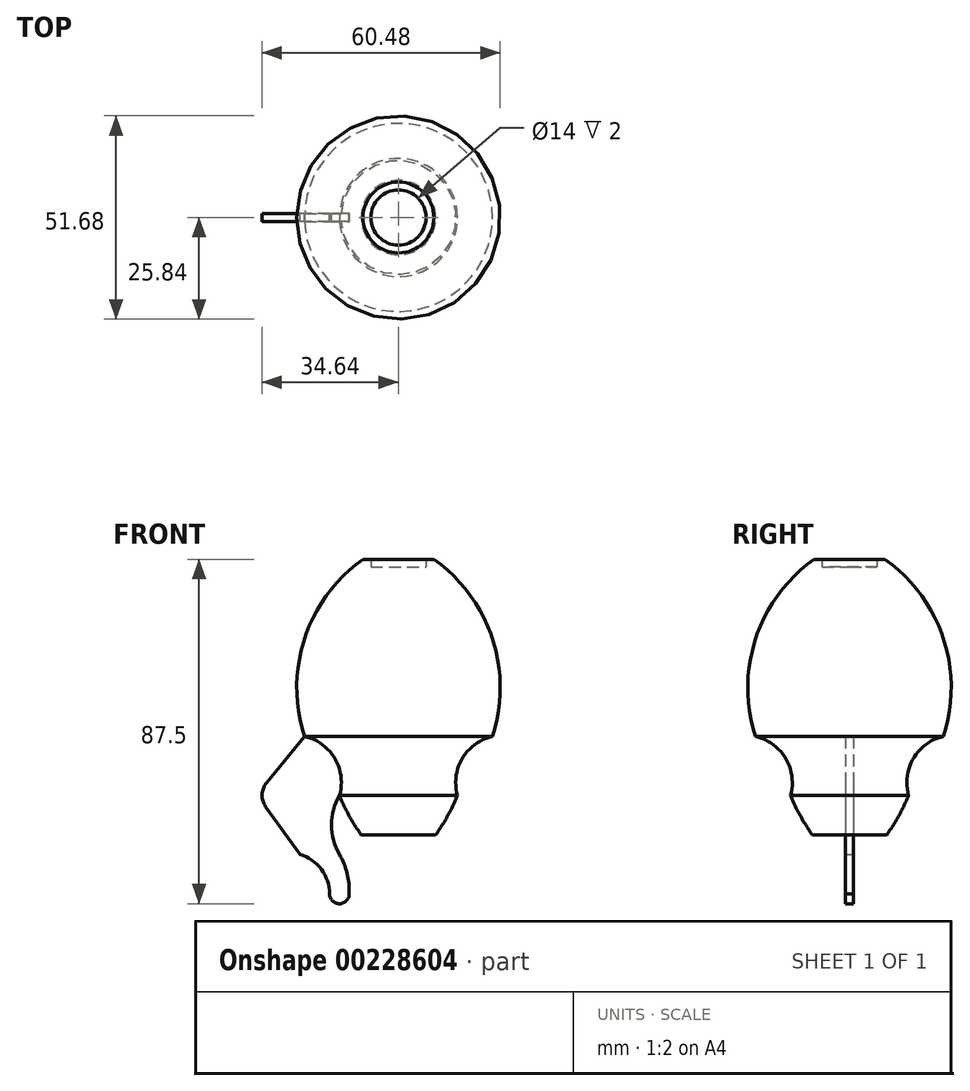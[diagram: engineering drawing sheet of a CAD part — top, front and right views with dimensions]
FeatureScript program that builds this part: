
annotation { "Feature Type Name" : "Feature", "Feature Type Description" : "" }
export const myFeature = defineFeature(function(context is Context, id is Id, definition is map)
    precondition{}
    {
        {
            var Q0;
            Q0=qCreatedBy(makeId("Front.planeOp"),FACE);
            var sketch = newSketch(context, id + "F0", { "sketchPlane" : qUnion([Q0])});
            skLineSegment(sketch, "E0", {"start": v(0, 0) * mm, "end": v(0, 78) * mm});
            skLineSegment(sketch, "E1", {"start": v(7, 80) * mm, "end": v(9, 80) * mm});
            skLineSegment(sketch, "E2", {"start": v(0, 20) * mm, "end": v(15, 20) * mm});
            skLineSegment(sketch, "E3", {"start": v(0, 35) * mm, "end": v(23.88, 35) * mm});
            skArc(sketch, "E4", {"start": v(23.88, 35) * mm, "mid": v(23.82, 59.94) * mm, "end": v(9, 80) * mm});
            skArc(sketch, "E5", {"start": v(23.88, 35) * mm, "mid": v(16.21, 29.41) * mm, "end": v(15, 20) * mm});
            skArc(sketch, "E6", {"start": v(0, 0) * mm, "mid": v(8.77, 9.05) * mm, "end": v(15, 20) * mm});
            skLineSegment(sketch, "E7", {"start": v(7, 80) * mm, "end": v(7, 78) * mm});
            skLineSegment(sketch, "E8", {"start": v(7, 78) * mm, "end": v(0, 78) * mm});
            skSolve(sketch);
        }
        {
            var Q0;
            Q0=makeQuery(id+"F0.imprint","IMPRINT",FACE,{"disambiguationData":[TD([[makeQuery(id+"F0.imprint","IMPRINT",EDGE,{"derivedFrom":sQuery(id+"F0.wireOp",EDGE,"E1")}),-1.0]])]});
            var Q1;
            {var subQ0=sQuery(id+"F0.wireOp",EDGE,"E2");Q1=makeQuery(id+"F0.imprint","IMPRINT",FACE,{"disambiguationData":[TD([[makeQuery(id+"F0.imprint","IMPRINT",EDGE,{"derivedFrom":subQ0}),1.0]])]});}
            var Q2;
            {var subQ2=sQuery(id+"F0.wireOp",EDGE,"E2");Q2=makeQuery(id+"F0.imprint","IMPRINT",FACE,{"disambiguationData":[TD([[makeQuery(id+"F0.imprint","IMPRINT",EDGE,{"derivedFrom":subQ2}),-1.0]])]});}
            var Q3;
            Q3=sQuery(id+"F0.wireOp",EDGE,"E0");
            revolve(context, id + "F1", {"entities" : qUnion([Q0, Q1, Q2]), "axis" : qUnion([Q3]), "revolveType" : RevolveType.FULL});
        }
        {
            var Q0;
            Q0=qCreatedBy(makeId("Front.planeOp"),FACE);
            var sketch = newSketch(context, id + "F2", { "sketchPlane" : qUnion([Q0])});
            skLineSegment(sketch, "E9.0", {"start": v(15, 20) * mm, "end": v(-15, 20) * mm});
            skLineSegment(sketch, "E10.0", {"start": v(23.88, 35) * mm, "end": v(-23.88, 35) * mm});
            skLineSegment(sketch, "E11", {"start": v(-23.88, 35) * mm, "end": v(-15, 20) * mm});
            skLineSegment(sketch, "E12", {"start": v(0, 35) * mm, "end": v(0, 20) * mm});
            skSolve(sketch);
        }
        {
            var Q0;
            Q0 = qSketchRegion(id + "F2", true);
            extrude(context, id + "F3", {"entities" : qUnion([Q0]), "operationType" : NewBodyOperationType.ADD, "endBound" : BoundingType.SYMMETRIC, "depth" : 2 * mm});
        }
        {
            var Q0;
            Q0=qCreatedBy(makeId("Front.planeOp"),FACE);
            var sketch = newSketch(context, id + "F4", { "sketchPlane" : qUnion([Q0])});
            skLineSegment(sketch, "E13", {"start": v(0, 0) * mm, "end": v(0, -5) * mm});
            skLineSegment(sketch, "E14", {"start": v(0, -5) * mm, "end": v(-15, -5) * mm});
            skLineSegment(sketch, "E15", {"start": v(-15, -5) * mm, "end": v(-15, 5) * mm});
            skArc(sketch, "E16", {"start": v(-17.5, -5) * mm, "mid": v(-15, -7.5) * mm, "end": v(-12.5, -5) * mm});
            skLineSegment(sketch, "E17", {"start": v(-15, -5) * mm, "end": v(-17.5, -5) * mm});
            skArc(sketch, "E18", {"start": v(-14.97, 20) * mm, "mid": v(-17, 12.5) * mm, "end": v(-15, 5) * mm});
            skArc(sketch, "E19", {"start": v(-12.5, -5) * mm, "mid": v(-13.05, 0.17) * mm, "end": v(-15, 5) * mm});
            skArc(sketch, "E20", {"start": v(-17.5, -5) * mm, "mid": v(-19.58, 1.25) * mm, "end": v(-25, 5) * mm});
            skLineSegment(sketch, "E21", {"start": v(-23.86, 35) * mm, "end": v(-33.5, 23.24) * mm});
            skLineSegment(sketch, "E22", {"start": v(-33.7, 17.16) * mm, "end": v(-25, 5) * mm});
            skPoint(sketch, "E23.visualSharp", {"position": v(-35.94, 20.27) * mm});
            skArc(sketch, "E23.filletArc", {"start": v(-33.5, 23.24) * mm, "mid": v(-34.64, 20.23) * mm, "end": v(-33.7, 17.16) * mm});
            skLineSegment(sketch, "E24.0", {"start": v(-23.88, 35) * mm, "end": v(-15, 20) * mm});
            skPoint(sketch, "E25.0.end.orphan", {"position": v(23.88, 35) * mm});
            skPoint(sketch, "E26.0.end.orphan", {"position": v(15, 20) * mm});
            skFitSpline(sketch, "E27.0", {"points": [v(-23.86, 35) * mm, v(-23.46, 34.91) * mm, v(-22.67, 34.69) * mm, v(-21.54, 34.24) * mm, v(-20.46, 33.68) * mm, v(-19.6, 33.13) * mm, v(-18.96, 32.63) * mm, v(-18.34, 32.1) * mm, v(-17.62, 31.39) * mm, v(-16.85, 30.45) * mm, v(-16.16, 29.42) * mm, v(-15.6, 28.35) * mm, v(-15.22, 27.4) * mm, v(-14.97, 26.63) * mm, v(-14.76, 25.84) * mm, v(-14.62, 25.04) * mm, v(-14.53, 24.22) * mm, v(-14.5, 23.4) * mm, v(-14.53, 21.98) * mm, v(-14.74, 20.79) * mm, v(-14.97, 20) * mm]});
            skSolve(sketch);
        }
        {
            var Q0;
            Q0 = qSketchRegion(id + "F4", true);
            extrude(context, id + "F5", {"entities" : qUnion([Q0]), "operationType" : NewBodyOperationType.ADD, "endBound" : BoundingType.SYMMETRIC, "depth" : 2 * mm});
        }
        {
            var Q0;
            Q0=qCreatedBy(makeId("Top.planeOp"),FACE);
            var sketch = newSketch(context, id + "F6", { "sketchPlane" : qUnion([Q0])});
            skCircle(sketch, "E28", {"center": v(0, 0) * mm, "radius": 10 * mm});
            skSolve(sketch);
        }
        {
            var Q0;
            Q0 = qSketchRegion(id + "F6", true);
            extrude(context, id + "F7", {"entities" : qUnion([Q0]), "operationType" : NewBodyOperationType.REMOVE, "depth" : 10 * mm});
        }
    });
